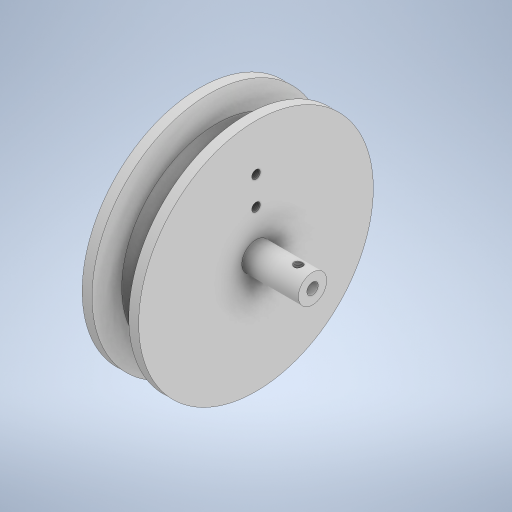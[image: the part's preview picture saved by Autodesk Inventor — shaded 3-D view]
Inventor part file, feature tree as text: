
AUTODESK INVENTOR PART (.ipt)
format: ipt  version: 2023 (Build 270158000, 158)  size: 315,904 bytes
history: native  units: mm
features: sketch x6, extrude x4, other x3, thread x3, revolve x1
ambient origin geometry x8: Origin, YZ Plane, XZ Plane, XY Plane, X Axis, Y Axis, Z Axis, Center Point
bodies: Body1 (feature_tree)
feature tree (17):
  other  "Твердое тело1"
  revolve  "Вращение1"
  extrude  "Выдавливание1"  Depth=20.0mm
  extrude  "Выдавливание2"  Depth=41.5mm
  sketch  "Эскиз4"
  other  "РабПлоскость1"
  extrude  "Выдавливание3"  Depth=6.0mm
  thread  "Резьба1"
  other  "РабПлоскость2"
  extrude  "Выдавливание4"  Depth=8.0mm
  thread  "Резьба2"
  thread  "Резьба3"
  sketch  "Эскиз1"
  sketch  "Эскиз2"
  sketch  "Эскиз3"
  sketch  "Эскиз5"
  sketch  "Эскиз6"
